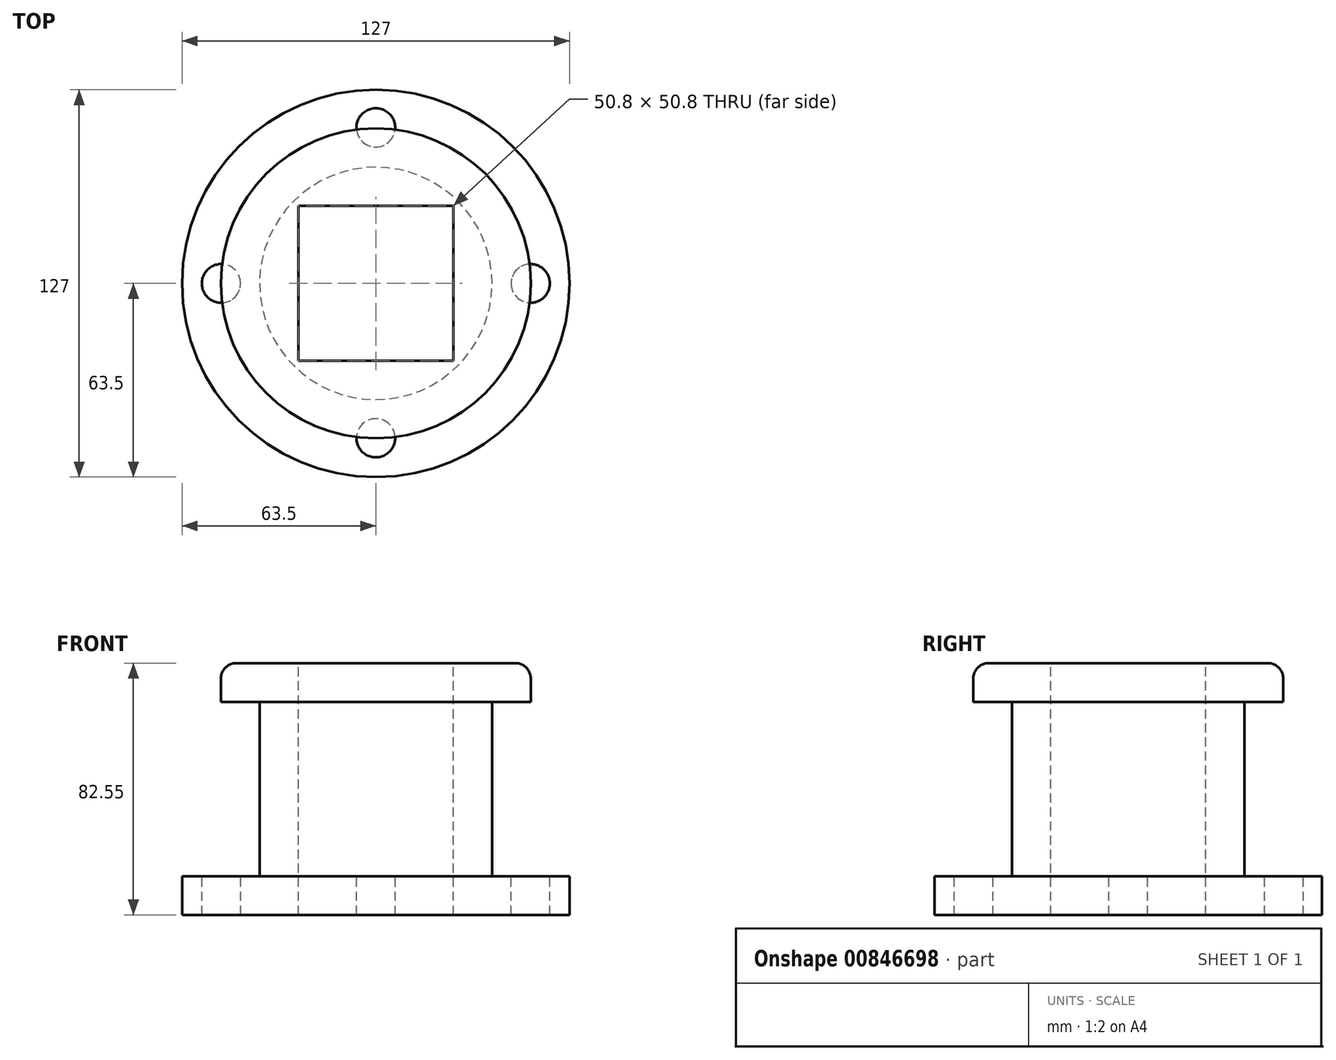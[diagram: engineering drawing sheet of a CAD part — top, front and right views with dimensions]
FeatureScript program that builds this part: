
annotation { "Feature Type Name" : "Feature", "Feature Type Description" : "" }
export const myFeature = defineFeature(function(context is Context, id is Id, definition is map)
    precondition{}
    {
        {
            var Q0;
            Q0=qCreatedBy(makeId("Top.planeOp"),FACE);
            var sketch = newSketch(context, id + "F0", { "sketchPlane" : qUnion([Q0])});
            skCircle(sketch, "E0", {"center": v(0, 0) * mm, "radius": 38.1 * mm});
            skSolve(sketch);
        }
        {
            var Q0;
            Q0 = qSketchRegion(id + "F0", true);
            extrude(context, id + "F1", {"entities" : qUnion([Q0]), "depth" : 57.15 * mm, "offsetDistance" : 25.4 * mm});
        }
        {
            var Q0;
            Q0=makeQuery(id+"F1.opExtrude","CAP_FACE",FACE,{"disambiguationData":[OSD([sQuery(id+"F0.wireOp",EDGE,"E0")])],"isStart":false});
            var sketch = newSketch(context, id + "F2", { "sketchPlane" : qUnion([Q0])});
            skCircle(sketch, "E1", {"center": v(0, 0) * mm, "radius": 50.8 * mm});
            skSolve(sketch);
        }
        {
            var Q0;
            Q0 = qSketchRegion(id + "F2", true);
            extrude(context, id + "F3", {"entities" : qUnion([Q0]), "operationType" : NewBodyOperationType.ADD, "depth" : 12.7 * mm, "offsetDistance" : 25.4 * mm});
        }
        {
            var Q0;
            Q0=makeQuery(id+"F1.opExtrude","CAP_FACE",FACE,{"disambiguationData":[OSD([sQuery(id+"F0.wireOp",EDGE,"E0")])],"isStart":true});
            var sketch = newSketch(context, id + "F4", { "sketchPlane" : qUnion([Q0])});
            skCircle(sketch, "E2", {"center": v(0, 0) * mm, "radius": 63.5 * mm});
            skSolve(sketch);
        }
        {
            var Q0;
            Q0 = qSketchRegion(id + "F4", true);
            extrude(context, id + "F5", {"entities" : qUnion([Q0]), "operationType" : NewBodyOperationType.ADD, "depth" : 12.7 * mm, "offsetDistance" : 25.4 * mm});
        }
        {
            var Q0;
            Q0=makeQuery(id+"F3.opExtrude","CAP_EDGE",EDGE,{"disambiguationData":[OSD([sQuery(id+"F2.wireOp",EDGE,"E1")])],"isStart":false});
            fillet(context, id + "F6", {"entities" : qUnion([Q0]), "radius" : 5.08 * mm, "tangentPropagation" : true, "allowEdgeOverflow" : false});
        }
        {
            var Q0;
            Q0=makeQuery(id+"F3.opExtrude","CAP_FACE",FACE,{"disambiguationData":[OSD([sQuery(id+"F2.wireOp",EDGE,"E1")])],"isStart":false});
            var sketch = newSketch(context, id + "F7", { "sketchPlane" : qUnion([Q0])});
            skLineSegment(sketch, "E3.bottom", {"start": v(25.4, 25.4) * mm, "end": v(-25.4, 25.4) * mm});
            skLineSegment(sketch, "E3.top", {"start": v(25.4, -25.4) * mm, "end": v(-25.4, -25.4) * mm});
            skLineSegment(sketch, "E3.left", {"start": v(25.4, 25.4) * mm, "end": v(25.4, -25.4) * mm});
            skLineSegment(sketch, "E3.right", {"start": v(-25.4, 25.4) * mm, "end": v(-25.4, -25.4) * mm});
            skPoint(sketch, "E3.middle", {"position": v(0, 0) * mm});
            skSolve(sketch);
        }
        {
            var Q0;
            Q0 = qSketchRegion(id + "F7", true);
            extrude(context, id + "F8", {"entities" : qUnion([Q0]), "operationType" : NewBodyOperationType.REMOVE, "oppositeDirection" : true, "depth" : 127 * mm, "offsetDistance" : 25.4 * mm});
        }
        {
            var Q0;
            Q0=makeQuery(id+"F5.opExtrude","CAP_FACE",FACE,{"disambiguationData":[OSD([sQuery(id+"F4.wireOp",EDGE,"E2")])],"isStart":true});
            var sketch = newSketch(context, id + "F9", { "sketchPlane" : qUnion([Q0])});
            skCircle(sketch, "E4", {"center": v(0, 51.08) * mm, "radius": 6.35 * mm});
            skCircle(sketch, "E5", {"center": v(50.7, 0) * mm, "radius": 6.35 * mm});
            skCircle(sketch, "E6", {"center": v(0, -50.7) * mm, "radius": 6.35 * mm});
            skCircle(sketch, "E7", {"center": v(-50.7, 0) * mm, "radius": 6.35 * mm});
            skSolve(sketch);
        }
        {
            var Q0;
            Q0 = qSketchRegion(id + "F9", true);
            extrude(context, id + "F10", {"entities" : qUnion([Q0]), "operationType" : NewBodyOperationType.REMOVE, "oppositeDirection" : true, "depth" : 25.4 * mm, "offsetDistance" : 25.4 * mm});
        }
    });
